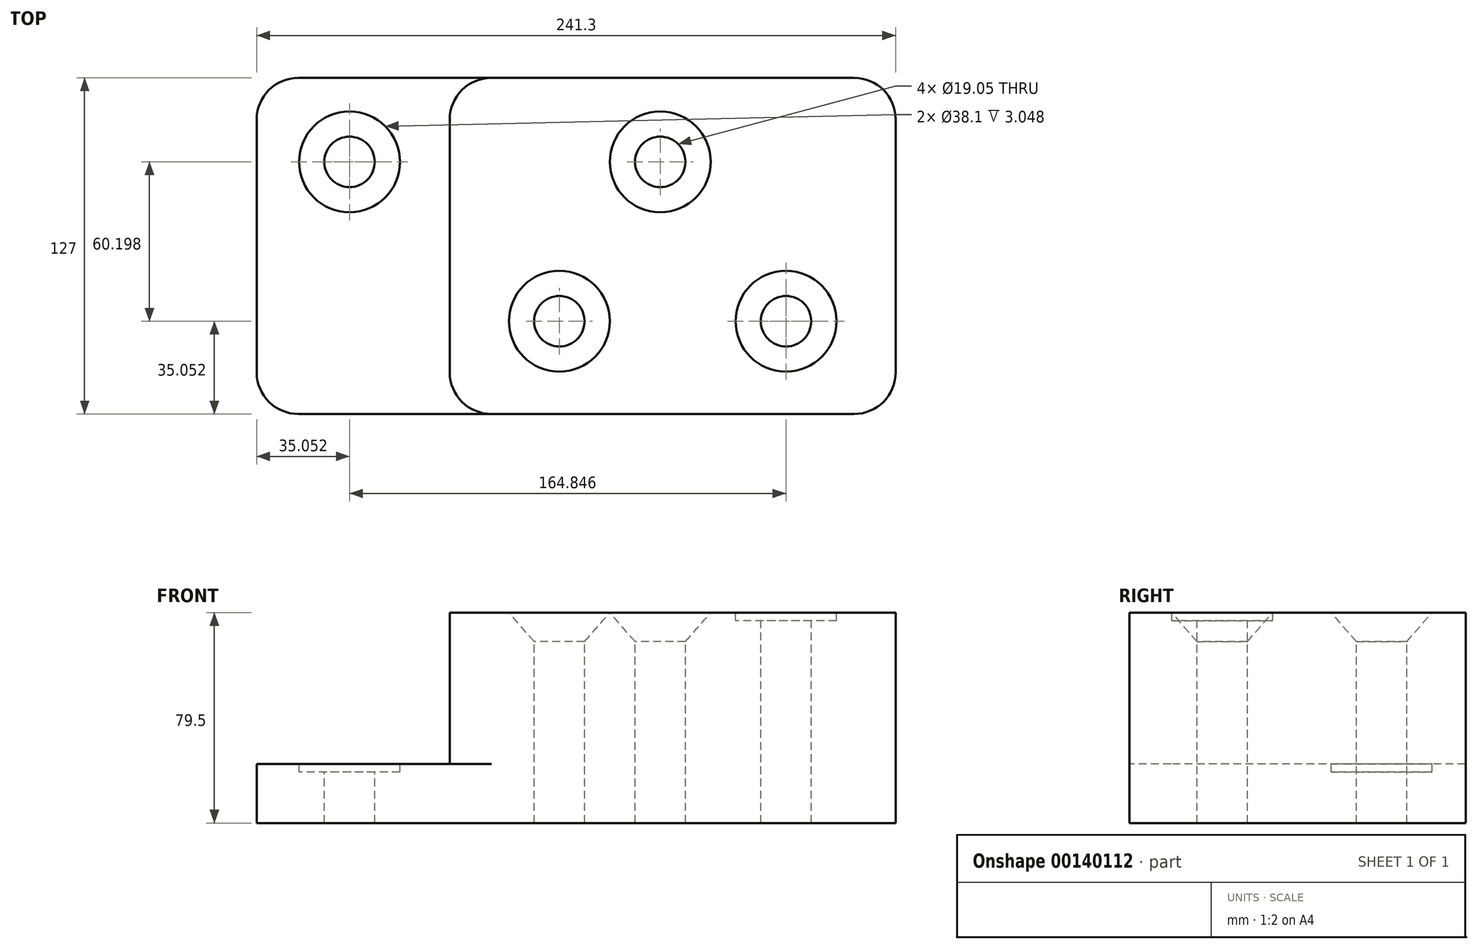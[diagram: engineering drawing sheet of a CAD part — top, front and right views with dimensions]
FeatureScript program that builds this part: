
annotation { "Feature Type Name" : "Feature", "Feature Type Description" : "" }
export const myFeature = defineFeature(function(context is Context, id is Id, definition is map)
    precondition{}
    {
        {
            var Q0;
            Q0=qCreatedBy(makeId("Top.planeOp"),FACE);
            var sketch = newSketch(context, id + "F0", { "sketchPlane" : qUnion([Q0])});
            skLineSegment(sketch, "E0", {"start": v(0, 0) * mm, "end": v(241.3, 0) * mm});
            skLineSegment(sketch, "E1", {"start": v(241.3, 0) * mm, "end": v(241.3, 127) * mm});
            skLineSegment(sketch, "E2", {"start": v(241.3, 127) * mm, "end": v(0, 127) * mm});
            skLineSegment(sketch, "E3", {"start": v(0, 127) * mm, "end": v(0, 0) * mm});
            skLineSegment(sketch, "E4", {"start": v(241.3, 127) * mm, "end": v(72.9, 127) * mm, "construction": true});
            skLineSegment(sketch, "E5", {"start": v(72.9, 127) * mm, "end": v(72.9, 0) * mm});
            skSolve(sketch);
        }
        {
            var Q0;
            {var subQ0=sQuery(id+"F0.wireOp",EDGE,"E1");Q0=makeQuery(id+"F0.imprint","IMPRINT",FACE,{"disambiguationData":[TD([[makeQuery(id+"F0.imprint","IMPRINT",EDGE,{"derivedFrom":subQ0}),1.0]])]});}
            extrude(context, id + "F1", {"entities" : qUnion([Q0]), "depth" : 79.5 * mm});
        }
        {
            var Q0;
            {var subQ0=sQuery(id+"F0.wireOp",EDGE,"E3");Q0=makeQuery(id+"F0.imprint","IMPRINT",FACE,{"disambiguationData":[TD([[makeQuery(id+"F0.imprint","IMPRINT",EDGE,{"derivedFrom":subQ0}),1.0]])]});}
            extrude(context, id + "F2", {"entities" : qUnion([Q0]), "operationType" : NewBodyOperationType.ADD, "depth" : 22.35 * mm});
        }
        {
            var Q0;
            Q0=makeQuery(id+"F1.opExtrude","CAP_FACE",FACE,{"disambiguationData":[OSD([sQuery(id+"F0.wireOp",EDGE,"E0"),sQuery(id+"F0.wireOp",EDGE,"E1"),sQuery(id+"F0.wireOp",EDGE,"E2"),sQuery(id+"F0.wireOp",EDGE,"E5")])],"isStart":false});
            var sketch = newSketch(context, id + "F3", { "sketchPlane" : qUnion([Q0])});
            skLineSegment(sketch, "E6", {"start": v(241.3, 0) * mm, "end": v(241.3, 35.05) * mm});
            skLineSegment(sketch, "E7", {"start": v(241.3, 35.05) * mm, "end": v(199.9, 35.05) * mm, "construction": true});
            skLineSegment(sketch, "E8", {"start": v(199.9, 35.05) * mm, "end": v(114.3, 35.05) * mm, "construction": true});
            skLineSegment(sketch, "E9", {"start": v(241.3, 0) * mm, "end": v(241.3, 95.25) * mm, "construction": true});
            skLineSegment(sketch, "E10", {"start": v(241.3, 95.25) * mm, "end": v(152.4, 95.25) * mm, "construction": true});
            skSolve(sketch);
        }
        {
            var Q0;
            Q0=sQuery(id+"F3.wireOp",VERTEX,"E10.end");
            var Q1;
            Q1=sQuery(id+"F3.wireOp",VERTEX,"E8.end");
            var Q2;
            Q2=makeQuery(id+"F1.opExtrude","SWEPT_BODY",BODY,{"disambiguationData":[OSD([sQuery(id+"F0.wireOp",EDGE,"E0"),sQuery(id+"F0.wireOp",EDGE,"E1"),sQuery(id+"F0.wireOp",EDGE,"E2"),sQuery(id+"F0.wireOp",EDGE,"E5")])]});
            hole(context, id + "F4", {"style" : HoleStyle.C_SINK, "endStyle" : HoleEndStyle.THROUGH, "holeDiameter" : 19.05 * mm, "cSinkDiameter" : 38.1 * mm, "cSinkAngle" : 82 * degree, "locations" : qUnion([Q0, Q1]), "scope" : qUnion([Q2]), "isTappedThrough" : true});
        }
        {
            var Q0;
            Q0=makeQuery(id+"F2.opExtrude","CAP_FACE",FACE,{"disambiguationData":[OSD([sQuery(id+"F0.wireOp",EDGE,"E0"),sQuery(id+"F0.wireOp",EDGE,"E2"),sQuery(id+"F0.wireOp",EDGE,"E3"),sQuery(id+"F0.wireOp",EDGE,"E5")])],"isStart":false});
            var sketch = newSketch(context, id + "F5", { "sketchPlane" : qUnion([Q0])});
            skLineSegment(sketch, "E11", {"start": v(0, 0) * mm, "end": v(0, 95.25) * mm, "construction": true});
            skLineSegment(sketch, "E12", {"start": v(0, 95.25) * mm, "end": v(35.05, 95.25) * mm, "construction": true});
            skSolve(sketch);
        }
        {
            var Q0;
            Q0=sQuery(id+"F3.wireOp",VERTEX,"E8.start");
            var Q1;
            Q1=sQuery(id+"F5.wireOp",VERTEX,"E12.end");
            var Q2;
            Q2=makeQuery(id+"F1.opExtrude","SWEPT_BODY",BODY,{"disambiguationData":[OSD([sQuery(id+"F0.wireOp",EDGE,"E0"),sQuery(id+"F0.wireOp",EDGE,"E1"),sQuery(id+"F0.wireOp",EDGE,"E2"),sQuery(id+"F0.wireOp",EDGE,"E5")])]});
            hole(context, id + "F6", {"style" : HoleStyle.C_BORE, "endStyle" : HoleEndStyle.THROUGH, "holeDiameter" : 19.05 * mm, "cBoreDiameter" : 38.1 * mm, "cBoreDepth" : 3.05 * mm, "locations" : qUnion([Q0, Q1]), "scope" : qUnion([Q2]), "isTappedThrough" : true});
        }
        {
            var Q0;
            Q0=makeQuery(id+"F2.opExtrude","SWEPT_EDGE",EDGE,{"disambiguationData":[OSD([sQuery(id+"F0.wireOp",EDGE,"E0"),sQuery(id+"F0.wireOp",EDGE,"E3")])]});
            var Q1;
            Q1=makeQuery(id+"F2.opExtrude","SWEPT_EDGE",EDGE,{"disambiguationData":[OSD([sQuery(id+"F0.wireOp",EDGE,"E2"),sQuery(id+"F0.wireOp",EDGE,"E3")])]});
            fillet(context, id + "F7", {"entities" : qUnion([Q0, Q1]), "radius" : 15.75 * mm, "tangentPropagation" : true, "allowEdgeOverflow" : false});
        }
        {
            var Q0;
            Q0=makeQuery(id+"F1.opExtrude","SWEPT_EDGE",EDGE,{"disambiguationData":[OSD([sQuery(id+"F0.wireOp",EDGE,"E2"),sQuery(id+"F0.wireOp",EDGE,"E5")])]});
            var Q1;
            Q1=makeQuery(id+"F1.opExtrude","SWEPT_EDGE",EDGE,{"disambiguationData":[OSD([sQuery(id+"F0.wireOp",EDGE,"E0"),sQuery(id+"F0.wireOp",EDGE,"E5")])]});
            var Q2;
            Q2=makeQuery(id+"F1.opExtrude","SWEPT_EDGE",EDGE,{"disambiguationData":[OSD([sQuery(id+"F0.wireOp",EDGE,"E0"),sQuery(id+"F0.wireOp",EDGE,"E1")])]});
            var Q3;
            Q3=makeQuery(id+"F1.opExtrude","SWEPT_EDGE",EDGE,{"disambiguationData":[OSD([sQuery(id+"F0.wireOp",EDGE,"E1"),sQuery(id+"F0.wireOp",EDGE,"E2")])]});
            fillet(context, id + "F8", {"entities" : qUnion([Q0, Q1, Q2, Q3]), "radius" : 15.75 * mm, "tangentPropagation" : true, "allowEdgeOverflow" : false});
        }
    });
